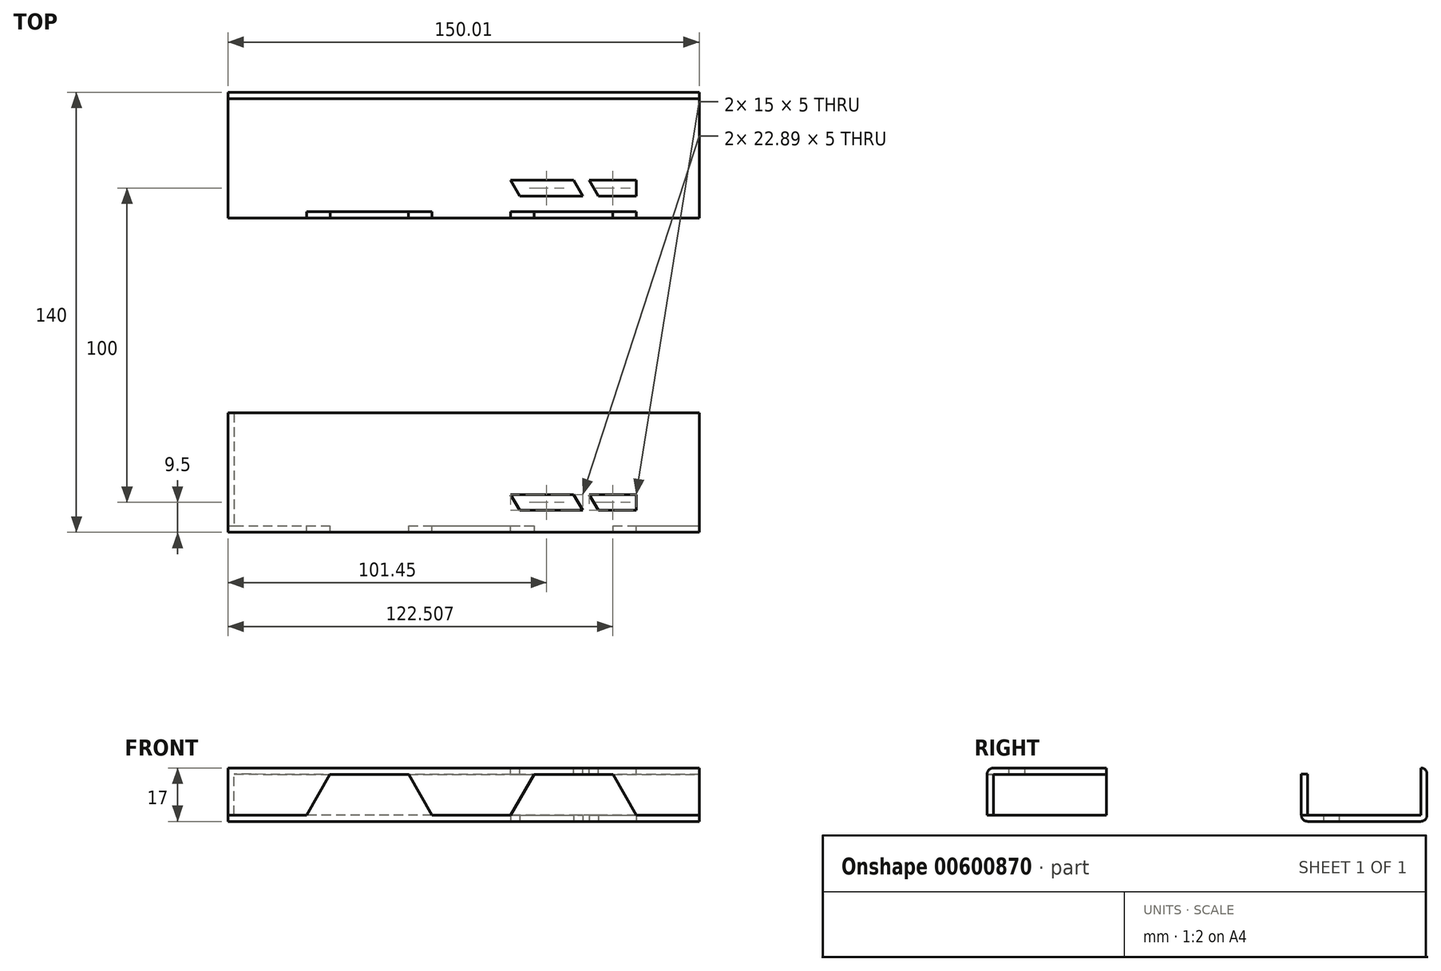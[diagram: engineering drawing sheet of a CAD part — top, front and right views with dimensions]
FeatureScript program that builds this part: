
annotation { "Feature Type Name" : "Feature", "Feature Type Description" : "" }
export const myFeature = defineFeature(function(context is Context, id is Id, definition is map)
    precondition{}
    {
        {
            var Q0;
            Q0=qCreatedBy(makeId("Front.planeOp"),FACE);
            var sketch = newSketch(context, id + "F0", { "sketchPlane" : qUnion([Q0])});
            skLineSegment(sketch, "E0.left", {"start": v(-101.93, 0.12) * mm, "end": v(-101.93, -12.88) * mm});
            skLineSegment(sketch, "E0.right", {"start": v(48.07, 0.12) * mm, "end": v(48.07, -12.88) * mm});
            skLineSegment(sketch, "E1", {"start": v(-76.93, -12.88) * mm, "end": v(-69.43, 0.12) * mm});
            skLineSegment(sketch, "E2", {"start": v(-44.44, 0.12) * mm, "end": v(-36.93, -12.88) * mm});
            skLineSegment(sketch, "E3", {"start": v(-11.94, -12.88) * mm, "end": v(-4.44, 0.12) * mm});
            skLineSegment(sketch, "E4", {"start": v(20.55, 0.12) * mm, "end": v(28.06, -12.88) * mm});
            skLineSegment(sketch, "E5.top", {"start": v(-101.93, 2.12) * mm, "end": v(48.07, 2.12) * mm});
            skLineSegment(sketch, "E5.left", {"start": v(-101.93, 0.12) * mm, "end": v(-101.93, 2.12) * mm});
            skLineSegment(sketch, "E5.right", {"start": v(48.07, 0.12) * mm, "end": v(48.07, 2.12) * mm});
            skLineSegment(sketch, "E6.top", {"start": v(-101.93, -14.88) * mm, "end": v(48.07, -14.88) * mm});
            skLineSegment(sketch, "E6.left", {"start": v(-101.93, -12.88) * mm, "end": v(-101.93, -14.88) * mm});
            skLineSegment(sketch, "E6.right", {"start": v(48.07, -12.88) * mm, "end": v(48.07, -14.88) * mm});
            skLineSegment(sketch, "E7", {"start": v(-76.93, -12.88) * mm, "end": v(-101.93, -12.88) * mm});
            skLineSegment(sketch, "E8", {"start": v(-36.93, -12.88) * mm, "end": v(-11.94, -12.88) * mm});
            skLineSegment(sketch, "E9", {"start": v(28.06, -12.88) * mm, "end": v(48.07, -12.88) * mm});
            skLineSegment(sketch, "E10", {"start": v(-69.43, 0.12) * mm, "end": v(-44.44, 0.12) * mm});
            skLineSegment(sketch, "E11", {"start": v(-4.44, 0.12) * mm, "end": v(20.55, 0.12) * mm});
            skSolve(sketch);
        }
        {
            var Q0;
            {var subQ1=sQuery(id+"F0.wireOp",EDGE,"E1");Q0=makeQuery(id+"F0.imprint","IMPRINT",FACE,{"disambiguationData":[TD([[makeQuery(id+"F0.imprint","IMPRINT",EDGE,{"derivedFrom":subQ1}),-1.0]])]});}
            extrude(context, id + "F1", {"entities" : qUnion([Q0]), "depth" : 2 * mm, "offsetDistance" : 25 * mm});
        }
        {
            var Q0;
            Q0=qCreatedBy(makeId("Front.planeOp"),FACE);
            cPlane(context, id + "F2", {"entities" : qUnion([Q0]), "cplaneType" : CPlaneType.OFFSET, "offset" : 100 * mm, "width" : 150 * mm, "height" : 150 * mm});
        }
        {
            var Q0;
            Q0=qCreatedBy(id+"F2.planeOp",FACE);
            var sketch = newSketch(context, id + "F3", { "sketchPlane" : qUnion([Q0])});
            skLineSegment(sketch, "E12.0.0", {"start": v(-101.93, -12.88) * mm, "end": v(-76.93, -12.88) * mm});
            skLineSegment(sketch, "E12.0.1", {"start": v(-76.93, -12.88) * mm, "end": v(-69.43, 0.12) * mm});
            skLineSegment(sketch, "E12.0.2", {"start": v(-69.43, 0.12) * mm, "end": v(-44.44, 0.12) * mm});
            skLineSegment(sketch, "E12.0.3", {"start": v(-44.44, 0.12) * mm, "end": v(-36.93, -12.88) * mm});
            skLineSegment(sketch, "E12.0.4", {"start": v(-36.93, -12.88) * mm, "end": v(-11.94, -12.88) * mm});
            skLineSegment(sketch, "E12.0.5", {"start": v(-11.94, -12.88) * mm, "end": v(-4.44, 0.12) * mm});
            skLineSegment(sketch, "E12.0.6", {"start": v(-4.44, 0.12) * mm, "end": v(20.55, 0.12) * mm});
            skLineSegment(sketch, "E12.0.7", {"start": v(20.55, 0.12) * mm, "end": v(28.06, -12.88) * mm});
            skLineSegment(sketch, "E12.0.8", {"start": v(28.06, -12.88) * mm, "end": v(48.07, -12.88) * mm});
            skLineSegment(sketch, "E12.0.9", {"start": v(48.07, -12.88) * mm, "end": v(48.07, 0.12) * mm});
            skLineSegment(sketch, "E12.0.10", {"start": v(48.07, 0.12) * mm, "end": v(48.07, 2.12) * mm});
            skLineSegment(sketch, "E12.0.11", {"start": v(48.07, 2.12) * mm, "end": v(-101.93, 2.12) * mm});
            skLineSegment(sketch, "E12.0.12", {"start": v(-101.93, 2.12) * mm, "end": v(-101.93, 0.12) * mm});
            skLineSegment(sketch, "E12.0.13", {"start": v(-101.93, 0.12) * mm, "end": v(-101.93, -12.88) * mm});
            skSolve(sketch);
        }
        {
            var Q0;
            Q0 = qSketchRegion(id + "F3", true);
            extrude(context, id + "F4", {"entities" : qUnion([Q0]), "depth" : 2 * mm, "offsetDistance" : 25 * mm});
        }
        {
            var Q0;
            Q0=makeQuery(id+"F0.imprint","IMPRINT",FACE,{"disambiguationData":[TD([[makeQuery(id+"F0.imprint","IMPRINT",EDGE,{"derivedFrom":sQuery(id+"F0.wireOp",EDGE,"E0.left")}),1.0]])]});
            cPlane(context, id + "F5", {"entities" : qUnion([Q0]), "cplaneType" : CPlaneType.OFFSET, "offset" : 38 * mm, "oppositeDirection" : true, "width" : 150 * mm, "height" : 150 * mm});
        }
        {
            var Q0;
            Q0=qCreatedBy(id+"F5.planeOp",FACE);
            var sketch = newSketch(context, id + "F6", { "sketchPlane" : qUnion([Q0])});
            skLineSegment(sketch, "E13.0.0", {"start": v(-69.43, 0.12) * mm, "end": v(-76.93, -12.88) * mm});
            skLineSegment(sketch, "E13.0.1", {"start": v(-76.93, -12.88) * mm, "end": v(-101.93, -12.88) * mm});
            skLineSegment(sketch, "E13.0.2", {"start": v(-101.93, -12.88) * mm, "end": v(-101.93, -14.88) * mm});
            skLineSegment(sketch, "E13.0.3", {"start": v(-101.93, -14.88) * mm, "end": v(48.07, -14.88) * mm});
            skLineSegment(sketch, "E13.0.4", {"start": v(48.07, -14.88) * mm, "end": v(48.07, -12.88) * mm});
            skLineSegment(sketch, "E13.0.5", {"start": v(48.07, -12.88) * mm, "end": v(28.06, -12.88) * mm});
            skLineSegment(sketch, "E13.0.6", {"start": v(28.06, -12.88) * mm, "end": v(20.55, 0.12) * mm});
            skLineSegment(sketch, "E13.0.7", {"start": v(20.55, 0.12) * mm, "end": v(-4.44, 0.12) * mm});
            skLineSegment(sketch, "E13.0.8", {"start": v(-4.44, 0.12) * mm, "end": v(-11.94, -12.88) * mm});
            skLineSegment(sketch, "E13.0.9", {"start": v(-11.94, -12.88) * mm, "end": v(-36.93, -12.88) * mm});
            skLineSegment(sketch, "E13.0.10", {"start": v(-36.93, -12.88) * mm, "end": v(-44.44, 0.12) * mm});
            skLineSegment(sketch, "E13.0.11", {"start": v(-44.44, 0.12) * mm, "end": v(-69.43, 0.12) * mm});
            skLineSegment(sketch, "E14", {"start": v(28.06, -12.88) * mm, "end": v(-76.93, -12.88) * mm});
            skSolve(sketch);
        }
        {
            var Q0;
            {var subQ1=sQuery(id+"F6.wireOp",EDGE,"E13.0.1");Q0=makeQuery(id+"F6.imprint","IMPRINT",FACE,{"disambiguationData":[TD([[makeQuery(id+"F6.imprint","IMPRINT",EDGE,{"derivedFrom":subQ1}),1.0]])]});}
            extrude(context, id + "F7", {"entities" : qUnion([Q0]), "operationType" : NewBodyOperationType.ADD, "endBound" : BoundingType.UP_TO_NEXT, "depth" : 15 * mm, "offsetDistance" : 25 * mm});
        }
        {
            var Q0;
            Q0=makeQuery(id+"F4.opExtrude","CAP_FACE",FACE,{"disambiguationData":[OSD([sQuery(id+"F3.wireOp",EDGE,"E12.0.0"),sQuery(id+"F3.wireOp",EDGE,"E12.0.1"),sQuery(id+"F3.wireOp",EDGE,"E12.0.2"),sQuery(id+"F3.wireOp",EDGE,"E12.0.3"),sQuery(id+"F3.wireOp",EDGE,"E12.0.4"),sQuery(id+"F3.wireOp",EDGE,"E12.0.5"),sQuery(id+"F3.wireOp",EDGE,"E12.0.6"),sQuery(id+"F3.wireOp",EDGE,"E12.0.7"),sQuery(id+"F3.wireOp",EDGE,"E12.0.8"),sQuery(id+"F3.wireOp",EDGE,"E12.0.9"),sQuery(id+"F3.wireOp",EDGE,"E12.0.10"),sQuery(id+"F3.wireOp",EDGE,"E12.0.11"),sQuery(id+"F3.wireOp",EDGE,"E12.0.12"),sQuery(id+"F3.wireOp",EDGE,"E12.0.13")])],"isStart":false});
            cPlane(context, id + "F8", {"entities" : qUnion([Q0]), "cplaneType" : CPlaneType.OFFSET, "offset" : 38 * mm, "oppositeDirection" : true, "width" : 150 * mm, "height" : 150 * mm});
        }
        {
            var Q0;
            Q0=qCreatedBy(id+"F8.planeOp",FACE);
            var sketch = newSketch(context, id + "F9", { "sketchPlane" : qUnion([Q0])});
            skLineSegment(sketch, "E15.0.0", {"start": v(-101.93, 2.12) * mm, "end": v(-101.93, -12.88) * mm});
            skLineSegment(sketch, "E15.0.1", {"start": v(-101.93, -12.88) * mm, "end": v(-76.93, -12.88) * mm});
            skLineSegment(sketch, "E15.0.2", {"start": v(-76.93, -12.88) * mm, "end": v(-69.43, 0.12) * mm});
            skLineSegment(sketch, "E15.0.4", {"start": v(-44.44, 0.12) * mm, "end": v(-36.93, -12.88) * mm});
            skLineSegment(sketch, "E15.0.5", {"start": v(-36.93, -12.88) * mm, "end": v(-11.94, -12.88) * mm});
            skLineSegment(sketch, "E15.0.6", {"start": v(-11.94, -12.88) * mm, "end": v(-4.44, 0.12) * mm});
            skLineSegment(sketch, "E15.0.8", {"start": v(20.55, 0.12) * mm, "end": v(28.06, -12.88) * mm});
            skLineSegment(sketch, "E15.0.9", {"start": v(28.06, -12.88) * mm, "end": v(48.07, -12.88) * mm});
            skLineSegment(sketch, "E15.0.10", {"start": v(48.07, -12.88) * mm, "end": v(48.07, 2.12) * mm});
            skLineSegment(sketch, "E15.0.11", {"start": v(48.07, 2.12) * mm, "end": v(-101.93, 2.12) * mm});
            skPoint(sketch, "E16.end.orphan", {"position": v(48.07, 0) * mm});
            skPoint(sketch, "E17.end.orphan", {"position": v(-101.93, 0.12) * mm});
            skLineSegment(sketch, "E18", {"start": v(48.07, 0) * mm, "end": v(-101.93, 0.12) * mm});
            skSolve(sketch);
        }
        {
            var Q0;
            {var subQ4=sQuery(id+"F9.wireOp",EDGE,"E15.0.11");Q0=makeQuery(id+"F9.imprint","IMPRINT",FACE,{"disambiguationData":[TD([[makeQuery(id+"F9.imprint","IMPRINT",EDGE,{"derivedFrom":subQ4}),1.0]])]});}
            extrude(context, id + "F10", {"entities" : qUnion([Q0]), "operationType" : NewBodyOperationType.ADD, "depth" : 38 * mm, "offsetDistance" : 25 * mm});
        }
        {
            var Q0;
            Q0=makeQuery(id+"F7.boolean.opBoolean","MERGE",FACE,{"derivedFrom":[makeQuery(id+"F1.opExtrude","SWEPT_FACE",FACE,{"disambiguationData":[OSD([sQuery(id+"F0.wireOp",EDGE,"E7")])]}),makeQuery(id+"F1.opExtrude","SWEPT_FACE",FACE,{"disambiguationData":[OSD([sQuery(id+"F0.wireOp",EDGE,"E8")])]}),makeQuery(id+"F1.opExtrude","SWEPT_FACE",FACE,{"disambiguationData":[OSD([sQuery(id+"F0.wireOp",EDGE,"E9")])]}),makeQuery(id+"F7.opExtrude","SWEPT_FACE",FACE,{"disambiguationData":[OSD([sQuery(id+"F6.wireOp",EDGE,"E13.0.1"),sQuery(id+"F6.wireOp",EDGE,"E13.0.5"),sQuery(id+"F6.wireOp",EDGE,"E14")])]})]});
            var sketch = newSketch(context, id + "F11", { "sketchPlane" : qUnion([Q0])});
            skLineSegment(sketch, "E19.bottom", {"start": v(48.07, 38) * mm, "end": v(-101.93, 38) * mm});
            skLineSegment(sketch, "E19.top", {"start": v(48.07, 36) * mm, "end": v(-101.93, 36) * mm});
            skLineSegment(sketch, "E19.left", {"start": v(48.07, 38) * mm, "end": v(48.07, 36) * mm});
            skLineSegment(sketch, "E19.right", {"start": v(-101.93, 38) * mm, "end": v(-101.93, 36) * mm});
            skSolve(sketch);
        }
        {
            var Q0;
            Q0=makeQuery(id+"F11.imprint","IMPRINT",FACE,{"disambiguationData":[TD([[makeQuery(id+"F11.imprint","IMPRINT",EDGE,{"derivedFrom":sQuery(id+"F11.wireOp",EDGE,"E19.bottom")}),1.0]])]});
            extrude(context, id + "F12", {"entities" : qUnion([Q0]), "operationType" : NewBodyOperationType.ADD, "depth" : 15 * mm, "offsetDistance" : 25 * mm});
        }
        {
            var Q0;
            Q0=makeQuery(id+"F10.opExtrude","SWEPT_FACE",FACE,{"disambiguationData":[OSD([sQuery(id+"F9.wireOp",EDGE,"E18")])]});
            var sketch = newSketch(context, id + "F13", { "sketchPlane" : qUnion([Q0])});
            skLineSegment(sketch, "E20.bottom", {"start": v(-101.93, 64) * mm, "end": v(-99.93, 64) * mm});
            skLineSegment(sketch, "E20.top", {"start": v(-101.93, 100) * mm, "end": v(-99.93, 100) * mm});
            skLineSegment(sketch, "E20.left", {"start": v(-101.93, 64) * mm, "end": v(-101.93, 100) * mm});
            skLineSegment(sketch, "E20.right", {"start": v(-99.93, 64) * mm, "end": v(-99.93, 100) * mm});
            skSolve(sketch);
        }
        {
            var Q0;
            Q0=makeQuery(id+"F13.imprint","IMPRINT",FACE,{"disambiguationData":[TD([[makeQuery(id+"F13.imprint","IMPRINT",EDGE,{"derivedFrom":sQuery(id+"F13.wireOp",EDGE,"E20.bottom")}),-1.0]])]});
            extrude(context, id + "F14", {"entities" : qUnion([Q0]), "operationType" : NewBodyOperationType.ADD, "depth" : 13 * mm, "offsetDistance" : 25 * mm});
        }
        {
            var Q0;
            Q0=makeQuery(id+"F10.boolean.opBoolean","MERGE",FACE,{"derivedFrom":[makeQuery(id+"F4.opExtrude","SWEPT_FACE",FACE,{"disambiguationData":[OSD([sQuery(id+"F3.wireOp",EDGE,"E12.0.11")])]}),makeQuery(id+"F10.opExtrude","SWEPT_FACE",FACE,{"disambiguationData":[OSD([sQuery(id+"F9.wireOp",EDGE,"E15.0.11")])]})]});
            var sketch = newSketch(context, id + "F15", { "sketchPlane" : qUnion([Q0])});
            skLineSegment(sketch, "E21.bottom", {"start": v(38.07, -90) * mm, "end": v(-11.93, -90) * mm});
            skLineSegment(sketch, "E21.top", {"start": v(38.07, -95) * mm, "end": v(-11.93, -95) * mm});
            skLineSegment(sketch, "E21.left", {"start": v(38.07, -90) * mm, "end": v(38.07, -95) * mm});
            skLineSegment(sketch, "E21.right", {"start": v(-11.93, -90) * mm, "end": v(-11.93, -95) * mm});
            skLineSegment(sketch, "E22", {"start": v(28.07, -90) * mm, "end": v(28.07, -95) * mm});
            skLineSegment(sketch, "E23", {"start": v(-11.93, -90) * mm, "end": v(-9.05, -95) * mm});
            skLineSegment(sketch, "E24", {"start": v(8.07, -90) * mm, "end": v(10.95, -95) * mm});
            skLineSegment(sketch, "E25", {"start": v(13.07, -90) * mm, "end": v(15.95, -95) * mm});
            skSolve(sketch);
        }
        {
            var Q0;
            {var subQ0=sQuery(id+"F15.wireOp",EDGE,"E23");Q0=makeQuery(id+"F15.imprint","IMPRINT",FACE,{"disambiguationData":[TD([[makeQuery(id+"F15.imprint","IMPRINT",EDGE,{"derivedFrom":subQ0}),1.0]])]});}
            var Q1;
            {var subQ0=sQuery(id+"F15.wireOp",EDGE,"E22");Q1=makeQuery(id+"F15.imprint","IMPRINT",FACE,{"disambiguationData":[TD([[makeQuery(id+"F15.imprint","IMPRINT",EDGE,{"derivedFrom":subQ0}),-1.0]])]});}
            extrude(context, id + "F16", {"entities" : qUnion([Q0, Q1]), "operationType" : NewBodyOperationType.REMOVE, "oppositeDirection" : true, "depth" : 25 * mm, "offsetDistance" : 25 * mm});
        }
        {
            var Q0;
            Q0=makeQuery(id+"F7.boolean.opBoolean","MERGE",FACE,{"derivedFrom":[makeQuery(id+"F1.opExtrude","SWEPT_FACE",FACE,{"disambiguationData":[OSD([sQuery(id+"F0.wireOp",EDGE,"E6.top")])]}),makeQuery(id+"F7.opExtrude","SWEPT_FACE",FACE,{"disambiguationData":[OSD([sQuery(id+"F6.wireOp",EDGE,"E13.0.3")])]})]});
            var sketch = newSketch(context, id + "F17", { "sketchPlane" : qUnion([Q0])});
            skLineSegment(sketch, "E26.bottom", {"start": v(-91.93, -10) * mm, "end": v(-41.93, -10) * mm});
            skLineSegment(sketch, "E26.top", {"start": v(-91.93, -5) * mm, "end": v(-41.93, -5) * mm});
            skLineSegment(sketch, "E26.left", {"start": v(-91.93, -10) * mm, "end": v(-91.93, -5) * mm});
            skLineSegment(sketch, "E26.right", {"start": v(-41.93, -10) * mm, "end": v(-41.93, -5) * mm});
            skLineSegment(sketch, "E27", {"start": v(-41.93, -10) * mm, "end": v(-44.82, -5) * mm});
            skLineSegment(sketch, "E28", {"start": v(-61.93, -10) * mm, "end": v(-64.82, -5) * mm});
            skLineSegment(sketch, "E29", {"start": v(-66.93, -10) * mm, "end": v(-69.82, -5) * mm});
            skLineSegment(sketch, "E30", {"start": v(-81.93, -5) * mm, "end": v(-81.93, -10) * mm});
            skLineSegment(sketch, "E31", {"start": v(-26.93, -38) * mm, "end": v(-26.93, 2) * mm});
            skLineSegment(sketch, "E32.MirrorCS", {"start": v(38.07, -10) * mm, "end": v(-11.93, -10) * mm});
            skLineSegment(sketch, "E33.MirrorCS", {"start": v(-11.93, -10) * mm, "end": v(-9.05, -5) * mm});
            skLineSegment(sketch, "E34.MirrorCS", {"start": v(38.07, -5) * mm, "end": v(-11.93, -5) * mm});
            skLineSegment(sketch, "E35.MirrorCS", {"start": v(8.07, -10) * mm, "end": v(10.95, -5) * mm});
            skLineSegment(sketch, "E36.MirrorCS", {"start": v(13.07, -10) * mm, "end": v(15.95, -5) * mm});
            skLineSegment(sketch, "E37.MirrorCS", {"start": v(28.07, -5) * mm, "end": v(28.07, -10) * mm});
            skSolve(sketch);
        }
        {
            var Q0;
            {var subQ0=sQuery(id+"F17.wireOp",EDGE,"E33.MirrorCS");Q0=makeQuery(id+"F17.imprint","IMPRINT",FACE,{"disambiguationData":[TD([[makeQuery(id+"F17.imprint","IMPRINT",EDGE,{"derivedFrom":subQ0}),-1.0]])]});}
            var Q1;
            {var subQ0=sQuery(id+"F17.wireOp",EDGE,"E36.MirrorCS");Q1=makeQuery(id+"F17.imprint","IMPRINT",FACE,{"disambiguationData":[TD([[makeQuery(id+"F17.imprint","IMPRINT",EDGE,{"derivedFrom":subQ0}),-1.0]])]});}
            extrude(context, id + "F18", {"entities" : qUnion([Q0, Q1]), "operationType" : NewBodyOperationType.REMOVE, "oppositeDirection" : true, "depth" : 25 * mm, "offsetDistance" : 25 * mm});
        }
        {
            var Q0;
            Q0=makeQuery(id+"F7.opExtrude","CAP_EDGE",EDGE,{"disambiguationData":[OSD([sQuery(id+"F6.wireOp",EDGE,"E13.0.3")])],"isStart":true});
            var Q1;
            Q1=makeQuery(id+"F4.opExtrude","CAP_EDGE",EDGE,{"disambiguationData":[OSD([sQuery(id+"F3.wireOp",EDGE,"E12.0.11")])],"isStart":false});
            var Q2;
            Q2=makeQuery(id+"F12.opExtrude","CAP_EDGE",EDGE,{"disambiguationData":[OSD([sQuery(id+"F11.wireOp",EDGE,"E19.bottom")])],"isStart":false});
            fillet(context, id + "F19", {"entities" : qUnion([Q0, Q1, Q2]), "radius" : 2 * mm, "tangentPropagation" : true, "allowEdgeOverflow" : false});
        }
        {
            var Q0;
            Q0=makeQuery(id+"F1.opExtrude","CAP_EDGE",EDGE,{"disambiguationData":[OSD([sQuery(id+"F0.wireOp",EDGE,"E6.top")])],"isStart":false});
            fillet(context, id + "F20", {"entities" : qUnion([Q0]), "radius" : 2 * mm, "tangentPropagation" : true, "allowEdgeOverflow" : false});
        }
    });
